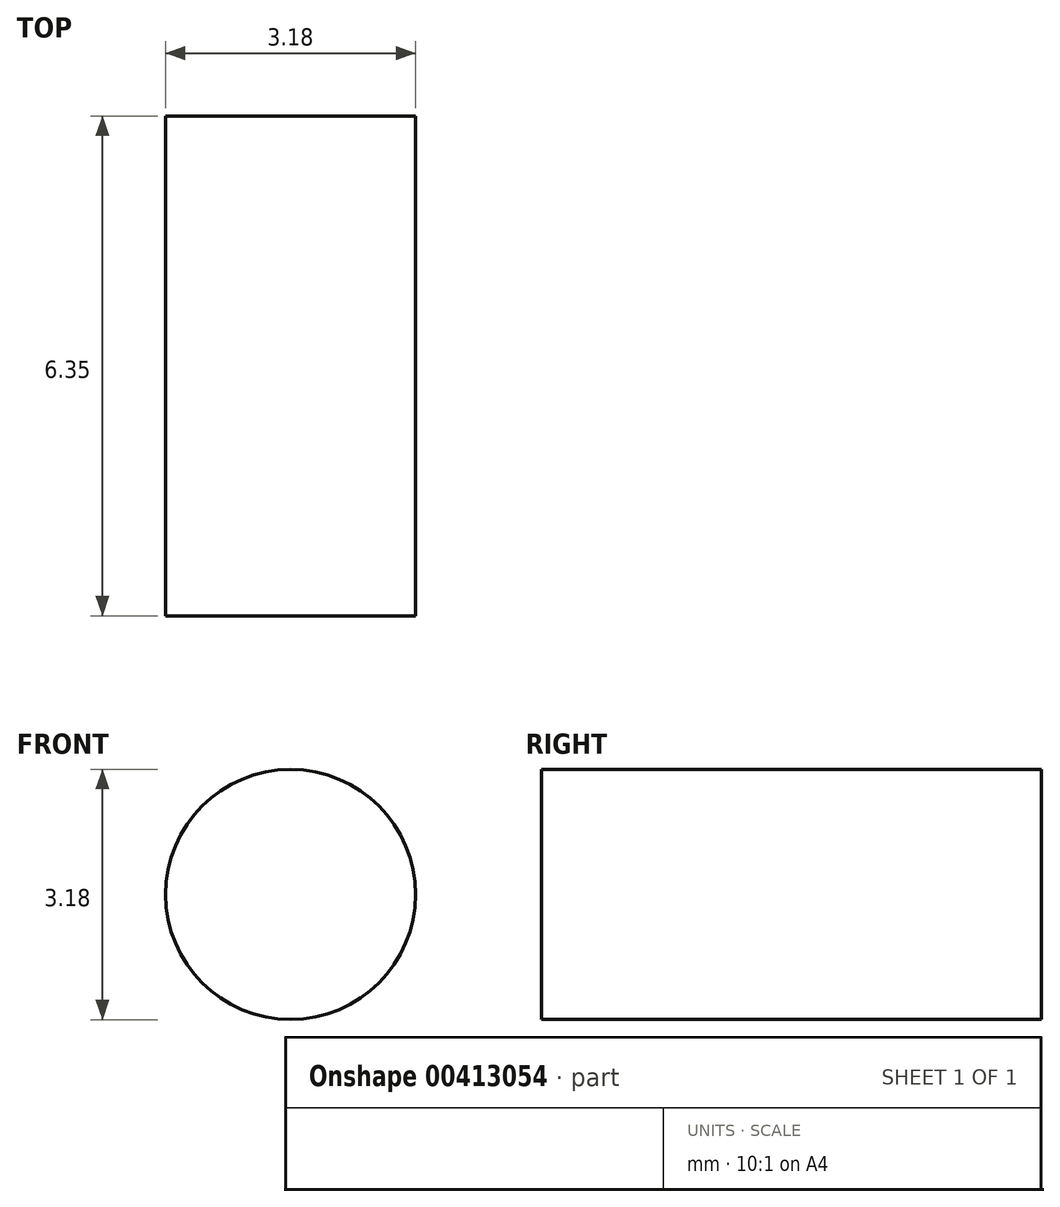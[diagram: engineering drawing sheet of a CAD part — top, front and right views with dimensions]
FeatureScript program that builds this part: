
annotation { "Feature Type Name" : "Feature", "Feature Type Description" : "" }
export const myFeature = defineFeature(function(context is Context, id is Id, definition is map)
    precondition{}
    {
        {
            var Q0;
            Q0=qCreatedBy(makeId("Front.planeOp"),FACE);
            var sketch = newSketch(context, id + "F0", { "sketchPlane" : qUnion([Q0])});
            skCircle(sketch, "E0", {"center": v(0, 0) * mm, "radius": 1.59 * mm});
            skSolve(sketch);
        }
        {
            var Q0;
            Q0 = qSketchRegion(id + "F0", true);
            extrude(context, id + "F1", {"entities" : qUnion([Q0]), "depth" : 6.35 * mm});
        }
    });
